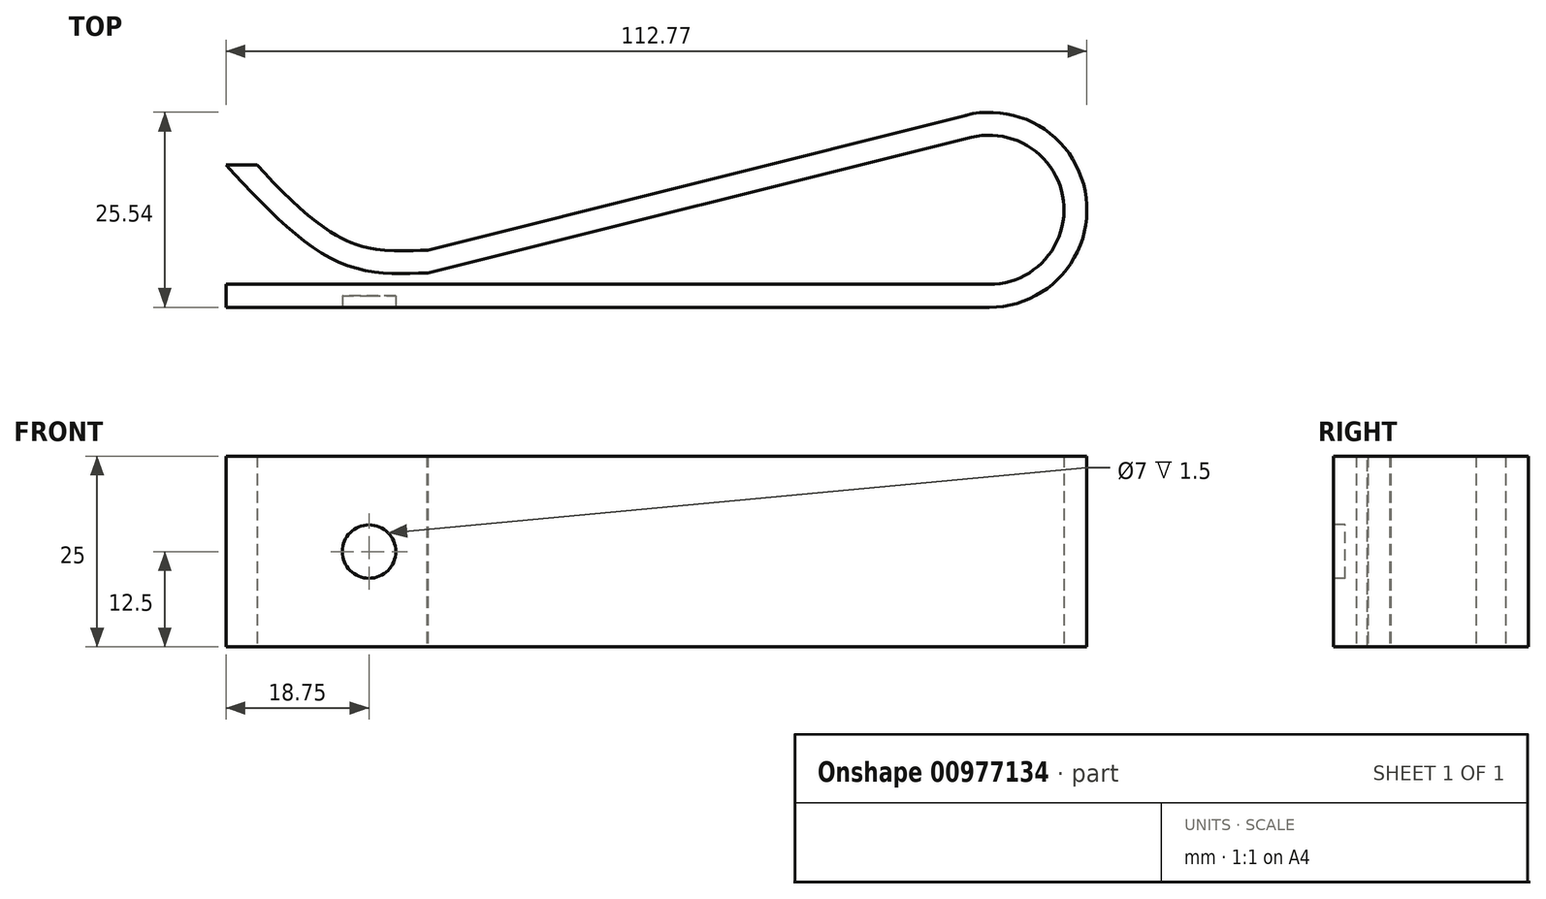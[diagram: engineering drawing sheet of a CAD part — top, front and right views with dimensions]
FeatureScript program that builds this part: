
annotation { "Feature Type Name" : "Feature", "Feature Type Description" : "" }
export const myFeature = defineFeature(function(context is Context, id is Id, definition is map)
    precondition{}
    {
        {
            var Q0;
            Q0=qCreatedBy(makeId("Top.planeOp"),FACE);
            var sketch = newSketch(context, id + "F0", { "sketchPlane" : qUnion([Q0])});
            skPoint(sketch, "E0", {"position": v(50, 0) * mm});
            skLineSegment(sketch, "E1", {"start": v(50, 0) * mm, "end": v(-50, 0) * mm});
            skLineSegment(sketch, "E2", {"start": v(-50, 0) * mm, "end": v(-50, 3) * mm});
            skLineSegment(sketch, "E3", {"start": v(-50, 3) * mm, "end": v(41.78, 3) * mm});
            skArc(sketch, "E4", {"start": v(50, 3) * mm, "mid": v(59.7, 13.96) * mm, "end": v(47.64, 22.25) * mm});
            skLineSegment(sketch, "E5", {"start": v(-23.58, 4.5) * mm, "end": v(39.66, 20.26) * mm});
            skLineSegment(sketch, "E6", {"start": v(-23.58, 7.5) * mm, "end": v(46.9, 25.15) * mm});
            skArc(sketch, "E7.trimOffspring", {"start": v(50, 0) * mm, "mid": v(62.67, 14.33) * mm, "end": v(46.9, 25.15) * mm});
            skFitSpline(sketch, "E8", {"points": [v(-23.58, 4.5) * mm, v(-35.25, 5.92) * mm, v(-50, 18.64) * mm], "startDerivative": vector(-26.8, -0.97) * mm, "endDerivative": vector(-26.07, 28.04) * mm});
            skFitSpline(sketch, "E9.0", {"points": [v(-23.69, 7.5) * mm, v(-24.8, 7.46) * mm, v(-26.96, 7.38) * mm, v(-29.45, 7.49) * mm, v(-31.34, 7.79) * mm, v(-32.48, 8.08) * mm, v(-33.37, 8.39) * mm, v(-34.04, 8.66) * mm, v(-34.72, 8.98) * mm, v(-35.65, 9.49) * mm, v(-36.85, 10.25) * mm, v(-38.83, 11.72) * mm, v(-41.4, 14) * mm, v(-44.56, 17.2) * mm, v(-46.72, 19.51) * mm, v(-47.8, 20.68) * mm]});
            skLineSegment(sketch, "E10", {"start": v(-23.69, 7.5) * mm, "end": v(-23.58, 7.5) * mm});
            skLineSegment(sketch, "E11", {"start": v(-50, 18.64) * mm, "end": v(-45.9, 18.64) * mm});
            skLineSegment(sketch, "E12", {"start": v(39.66, 20.26) * mm, "end": v(44.94, 21.57) * mm});
            skLineSegment(sketch, "E13", {"start": v(41.78, 3) * mm, "end": v(48.29, 3) * mm});
            skLineSegment(sketch, "E14", {"start": v(48.29, 3) * mm, "end": v(50, 3) * mm});
            skLineSegment(sketch, "E15", {"start": v(44.94, 21.57) * mm, "end": v(47.64, 22.25) * mm});
            skSolve(sketch);
        }
        {
            var Q0;
            Q0 = qSketchRegion(id + "F0", true);
            extrude(context, id + "F1", {"entities" : qUnion([Q0]), "depth" : 25 * mm, "offsetDistance" : 25.4 * mm});
        }
        {
            var Q0;
            Q0=makeQuery(id+"F1.opExtrude","SWEPT_FACE",FACE,{"disambiguationData":[OSD([sQuery(id+"F0.wireOp",EDGE,"E1")])]});
            var sketch = newSketch(context, id + "F2", { "sketchPlane" : qUnion([Q0])});
            skPoint(sketch, "E16", {"position": v(0, 25) * mm});
            skPoint(sketch, "E17", {"position": v(-50, 12.5) * mm});
            skLineSegment(sketch, "E18", {"start": v(0, 25) * mm, "end": v(0, 0) * mm});
            skLineSegment(sketch, "E19", {"start": v(-50, 12.5) * mm, "end": v(50, 12.5) * mm});
            skLineSegment(sketch, "E20.bottom", {"start": v(12.5, -17.5) * mm, "end": v(-12.5, -17.5) * mm});
            skLineSegment(sketch, "E20.top", {"start": v(12.5, 42.5) * mm, "end": v(-12.5, 42.5) * mm});
            skLineSegment(sketch, "E20.left", {"start": v(12.5, -17.5) * mm, "end": v(12.5, 42.5) * mm});
            skLineSegment(sketch, "E20.right", {"start": v(-12.5, -17.5) * mm, "end": v(-12.5, 42.5) * mm});
            skPoint(sketch, "E20.middle", {"position": v(0, 12.5) * mm});
            skPoint(sketch, "E21", {"position": v(12.5, 12.5) * mm});
            skPoint(sketch, "E22", {"position": v(-12.5, 12.5) * mm});
            skLineSegment(sketch, "E23", {"start": v(12.5, 12.5) * mm, "end": v(12.5, 42.5) * mm});
            skPoint(sketch, "E24", {"position": v(12.5, 27.5) * mm});
            skPoint(sketch, "E25", {"position": v(0, 27.5) * mm});
            skCircle(sketch, "E26", {"center": v(0, 27.5) * mm, "radius": 3.5 * mm});
            skCircle(sketch, "E27.MirrorC", {"center": v(0, -2.5) * mm, "radius": 3.5 * mm});
            skPoint(sketch, "E28", {"position": v(50, 12.5) * mm});
            skLineSegment(sketch, "E29", {"start": v(12.5, 12.5) * mm, "end": v(50, 12.5) * mm});
            skPoint(sketch, "E30", {"position": v(31.25, 12.5) * mm});
            skCircle(sketch, "E31", {"center": v(31.25, 12.5) * mm, "radius": 3.5 * mm});
            skCircle(sketch, "E32.MirrorC", {"center": v(-31.25, 12.5) * mm, "radius": 3.5 * mm});
            skSolve(sketch);
        }
        {
            var Q0;
            {var subQ0=sQuery(id+"F2.wireOp",EDGE,"E31");var subQ1=sQuery(id+"F2.wireOp",EDGE,"E29");var subQ2=makeQuery(id+"F2.imprint","INTERSECT",VERTEX,{"disambiguationData":[OD(0.0)],"derivedFrom":[subQ1,subQ0]});Q0=makeQuery(id+"F2.imprint","IMPRINT",FACE,{"disambiguationData":[TD([[makeQuery(id+"F2.imprint","IMPRINT",EDGE,{"disambiguationData":[TD([[subQ2,-1.0]])],"derivedFrom":subQ1}),1.0]])]});}
            var Q1;
            {var subQ0=sQuery(id+"F2.wireOp",EDGE,"E31");var subQ1=sQuery(id+"F2.wireOp",EDGE,"E29");var subQ2=makeQuery(id+"F2.imprint","INTERSECT",VERTEX,{"disambiguationData":[OD(0.0)],"derivedFrom":[subQ1,subQ0]});Q1=makeQuery(id+"F2.imprint","IMPRINT",FACE,{"disambiguationData":[TD([[makeQuery(id+"F2.imprint","IMPRINT",EDGE,{"disambiguationData":[TD([[subQ2,-1.0]])],"derivedFrom":subQ1}),-1.0]])]});}
            var Q2;
            {var subQ0=sQuery(id+"F2.wireOp",EDGE,"E32.MirrorC");var subQ1=sQuery(id+"F2.wireOp",EDGE,"E19");var subQ2=makeQuery(id+"F2.imprint","INTERSECT",VERTEX,{"disambiguationData":[OD(0.0)],"derivedFrom":[subQ1,subQ0]});Q2=makeQuery(id+"F2.imprint","IMPRINT",FACE,{"disambiguationData":[TD([[makeQuery(id+"F2.imprint","IMPRINT",EDGE,{"disambiguationData":[TD([[subQ2,-1.0]])],"derivedFrom":subQ1}),1.0]])]});}
            var Q3;
            {var subQ0=sQuery(id+"F2.wireOp",EDGE,"E32.MirrorC");var subQ1=sQuery(id+"F2.wireOp",EDGE,"E19");var subQ2=makeQuery(id+"F2.imprint","INTERSECT",VERTEX,{"disambiguationData":[OD(0.0)],"derivedFrom":[subQ1,subQ0]});Q3=makeQuery(id+"F2.imprint","IMPRINT",FACE,{"disambiguationData":[TD([[makeQuery(id+"F2.imprint","IMPRINT",EDGE,{"disambiguationData":[TD([[subQ2,-1.0]])],"derivedFrom":subQ1}),-1.0]])]});}
            extrude(context, id + "F3", {"entities" : qUnion([Q0, Q1, Q2, Q3]), "operationType" : NewBodyOperationType.REMOVE, "oppositeDirection" : true, "depth" : 1.5 * mm, "offsetDistance" : 25.4 * mm});
        }
    });
